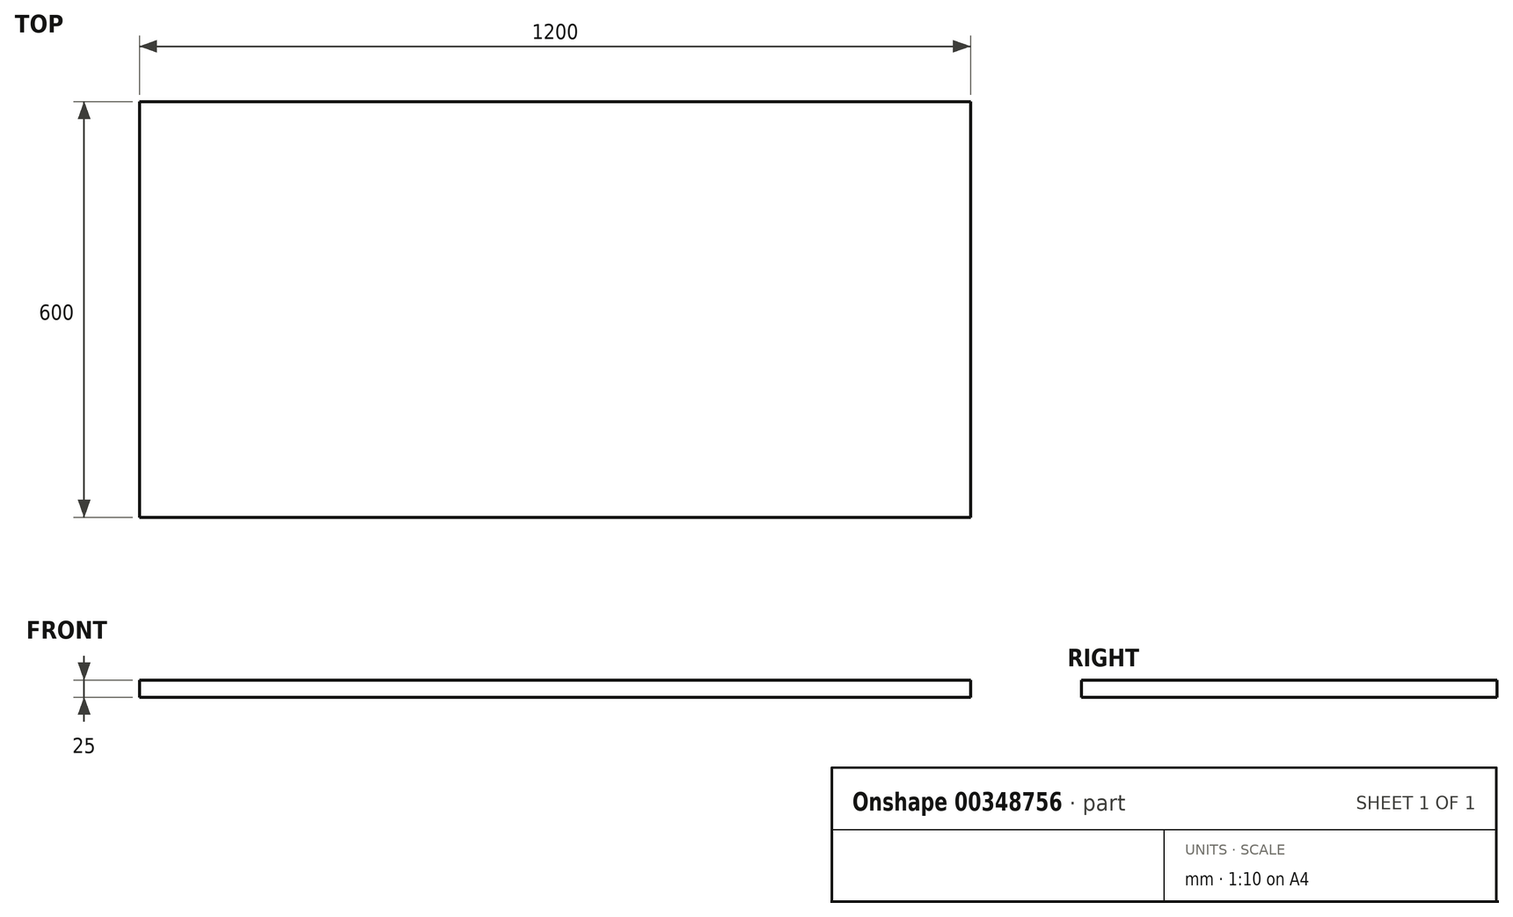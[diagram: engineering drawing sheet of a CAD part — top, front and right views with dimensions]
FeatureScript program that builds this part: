
annotation { "Feature Type Name" : "Feature", "Feature Type Description" : "" }
export const myFeature = defineFeature(function(context is Context, id is Id, definition is map)
    precondition{}
    {
        {
            var Q0;
            Q0=qCreatedBy(makeId("Top.planeOp"),FACE);
            var sketch = newSketch(context, id + "F0", { "sketchPlane" : qUnion([Q0])});
            skLineSegment(sketch, "E0.bottom", {"start": v(535.93, -262.53) * mm, "end": v(-664.07, -262.53) * mm});
            skLineSegment(sketch, "E0.top", {"start": v(535.93, 337.47) * mm, "end": v(-664.07, 337.47) * mm});
            skLineSegment(sketch, "E0.left", {"start": v(535.93, -262.53) * mm, "end": v(535.93, 337.47) * mm});
            skLineSegment(sketch, "E0.right", {"start": v(-664.07, -262.53) * mm, "end": v(-664.07, 337.47) * mm});
            skPoint(sketch, "E0.middle", {"position": v(-64.07, 37.47) * mm});
            skSolve(sketch);
        }
        {
            var Q0;
            Q0 = qSketchRegion(id + "F0", true);
            extrude(context, id + "F1", {"entities" : qUnion([Q0]), "depth" : 25 * mm});
        }
    });
